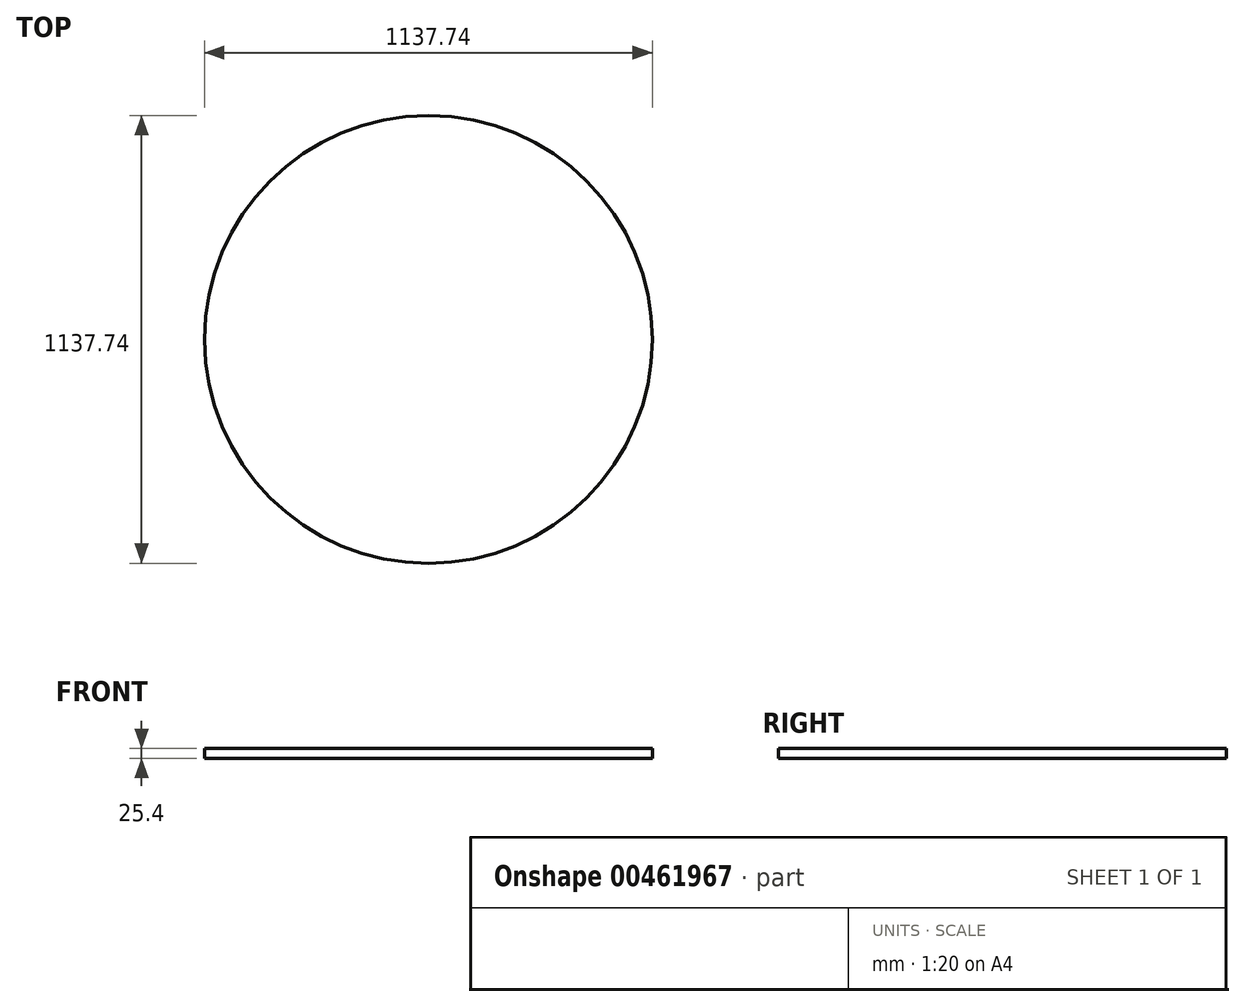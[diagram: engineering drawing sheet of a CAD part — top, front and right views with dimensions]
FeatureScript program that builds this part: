
annotation { "Feature Type Name" : "Feature", "Feature Type Description" : "" }
export const myFeature = defineFeature(function(context is Context, id is Id, definition is map)
    precondition{}
    {
        {
            var Q0;
            Q0=qCreatedBy(makeId("Top.planeOp"),FACE);
            var sketch = newSketch(context, id + "F0", { "sketchPlane" : qUnion([Q0])});
            skCircle(sketch, "E0", {"center": v(0, 0) * mm, "radius": 568.87 * mm});
            skSolve(sketch);
        }
        {
            var Q0;
            Q0=makeQuery(id+"F0.imprint","IMPRINT",FACE,{"disambiguationData":[TD([[makeQuery(id+"F0.imprint","IMPRINT",EDGE,{"derivedFrom":sQuery(id+"F0.wireOp",EDGE,"E0")}),1.0]])]});
            extrude(context, id + "F1", {"entities" : qUnion([Q0]), "depth" : 25.4 * mm});
        }
    });
